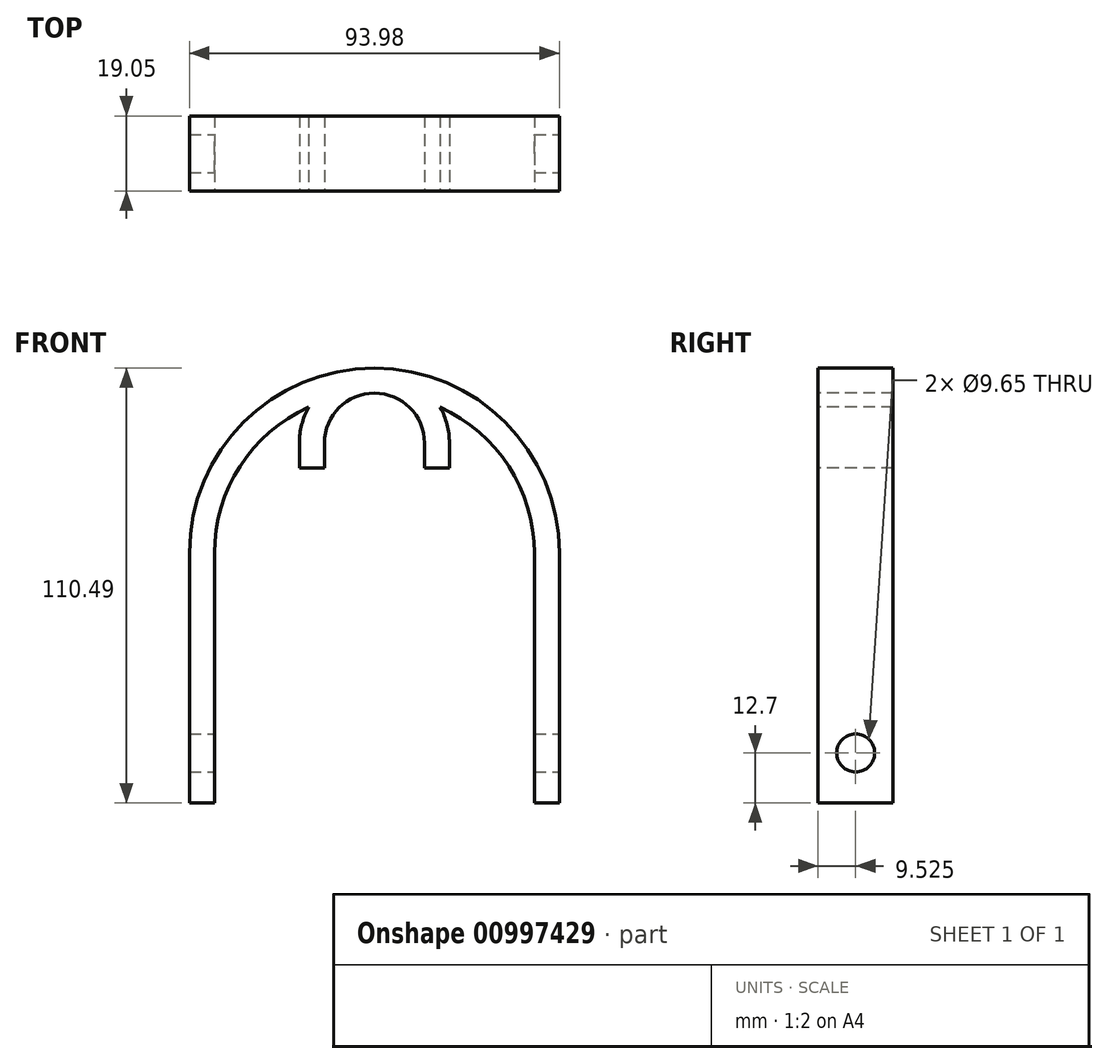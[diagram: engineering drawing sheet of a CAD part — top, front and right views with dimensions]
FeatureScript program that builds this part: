
annotation { "Feature Type Name" : "Feature", "Feature Type Description" : "" }
export const myFeature = defineFeature(function(context is Context, id is Id, definition is map)
    precondition{}
    {
        {
            var Q0;
            Q0=qCreatedBy(makeId("Front.planeOp"),FACE);
            var sketch = newSketch(context, id + "F0", { "sketchPlane" : qUnion([Q0])});
            skLineSegment(sketch, "E0", {"start": v(-40.64, 0) * mm, "end": v(40.64, 0) * mm});
            skArc(sketch, "E1", {"start": v(40.64, 0) * mm, "mid": v(0, 40.64) * mm, "end": v(-40.64, 0) * mm});
            skLineSegment(sketch, "E2.top", {"start": v(-40.64, -63.5) * mm, "end": v(40.64, -63.5) * mm});
            skLineSegment(sketch, "E2.left", {"start": v(-40.64, 0) * mm, "end": v(-40.64, -63.5) * mm});
            skLineSegment(sketch, "E2.right", {"start": v(40.64, 0) * mm, "end": v(40.64, -63.5) * mm});
            skLineSegment(sketch, "E3.0", {"start": v(47, 0) * mm, "end": v(47, -63.5) * mm});
            skArc(sketch, "E3.1", {"start": v(47, 0) * mm, "mid": v(0, 47) * mm, "end": v(-47, 0) * mm});
            skLineSegment(sketch, "E3.2", {"start": v(-47, 0) * mm, "end": v(-47, -63.5) * mm});
            skLineSegment(sketch, "E4", {"start": v(47, -63.5) * mm, "end": v(40.64, -63.5) * mm});
            skLineSegment(sketch, "E5", {"start": v(-40.64, -63.5) * mm, "end": v(-47, -63.5) * mm});
            skArc(sketch, "E6", {"start": v(12.7, 27.94) * mm, "mid": v(0, 40.64) * mm, "end": v(-12.7, 27.94) * mm});
            skArc(sketch, "E7.0", {"start": v(19.05, 27.94) * mm, "mid": v(0, 47) * mm, "end": v(-19.05, 27.94) * mm});
            skLineSegment(sketch, "E8", {"start": v(-19.05, 27.94) * mm, "end": v(-12.7, 27.94) * mm});
            skLineSegment(sketch, "E9", {"start": v(12.7, 27.94) * mm, "end": v(19.05, 27.94) * mm});
            skLineSegment(sketch, "E10.top", {"start": v(-19.05, 21.59) * mm, "end": v(-12.7, 21.59) * mm});
            skLineSegment(sketch, "E10.left", {"start": v(-19.05, 27.94) * mm, "end": v(-19.05, 21.59) * mm});
            skLineSegment(sketch, "E10.right", {"start": v(-12.7, 27.94) * mm, "end": v(-12.7, 21.59) * mm});
            skLineSegment(sketch, "E11.top", {"start": v(12.7, 21.6) * mm, "end": v(19.05, 21.6) * mm});
            skLineSegment(sketch, "E11.left", {"start": v(12.7, 27.94) * mm, "end": v(12.7, 21.6) * mm});
            skLineSegment(sketch, "E11.right", {"start": v(19.05, 27.94) * mm, "end": v(19.05, 21.6) * mm});
            skSolve(sketch);
        }
        {
            var Q0;
            {var subQ4=sQuery(id+"F0.wireOp",EDGE,"E2.left");Q0=makeQuery(id+"F0.imprint","IMPRINT",FACE,{"disambiguationData":[TD([[makeQuery(id+"F0.imprint","IMPRINT",EDGE,{"derivedFrom":subQ4}),-1.0]])]});}
            var Q1;
            {var subQ0=sQuery(id+"F0.wireOp",EDGE,"E7.0");var subQ1=sQuery(id+"F0.wireOp",EDGE,"E1");var subQ2=makeQuery(id+"F0.imprint","INTERSECT",VERTEX,{"disambiguationData":[OD(0.0)],"derivedFrom":[subQ1,subQ0]});Q1=makeQuery(id+"F0.imprint","IMPRINT",FACE,{"disambiguationData":[TD([[makeQuery(id+"F0.imprint","IMPRINT",EDGE,{"disambiguationData":[TD([[subQ2,-1.0]])],"derivedFrom":subQ1}),-1.0]])]});}
            var Q2;
            {var subQ4=sQuery(id+"F0.wireOp",EDGE,"E2.right");Q2=makeQuery(id+"F0.imprint","IMPRINT",FACE,{"disambiguationData":[TD([[makeQuery(id+"F0.imprint","IMPRINT",EDGE,{"derivedFrom":subQ4}),1.0]])]});}
            var Q3;
            {var subQ5=sQuery(id+"F0.wireOp",EDGE,"E9");Q3=makeQuery(id+"F0.imprint","IMPRINT",FACE,{"disambiguationData":[TD([[makeQuery(id+"F0.imprint","IMPRINT",EDGE,{"derivedFrom":subQ5}),1.0]])]});}
            var Q4;
            {var subQ5=sQuery(id+"F0.wireOp",EDGE,"E8");Q4=makeQuery(id+"F0.imprint","IMPRINT",FACE,{"disambiguationData":[TD([[makeQuery(id+"F0.imprint","IMPRINT",EDGE,{"derivedFrom":subQ5}),1.0]])]});}
            var Q5;
            {var subQ5=sQuery(id+"F0.wireOp",EDGE,"E8");Q5=makeQuery(id+"F0.imprint","IMPRINT",FACE,{"disambiguationData":[TD([[makeQuery(id+"F0.imprint","IMPRINT",EDGE,{"derivedFrom":subQ5}),1.0]])]});}
            var Q6;
            {var subQ5=sQuery(id+"F0.wireOp",EDGE,"E9");Q6=makeQuery(id+"F0.imprint","IMPRINT",FACE,{"disambiguationData":[TD([[makeQuery(id+"F0.imprint","IMPRINT",EDGE,{"derivedFrom":subQ5}),1.0]])]});}
            var Q7;
            Q7=makeQuery(id+"F0.imprint","IMPRINT",FACE,{"disambiguationData":[TD([[makeQuery(id+"F0.imprint","IMPRINT",EDGE,{"derivedFrom":sQuery(id+"F0.wireOp",EDGE,"E9")}),-1.0]])]});
            var Q8;
            Q8=makeQuery(id+"F0.imprint","IMPRINT",FACE,{"disambiguationData":[TD([[makeQuery(id+"F0.imprint","IMPRINT",EDGE,{"derivedFrom":sQuery(id+"F0.wireOp",EDGE,"E8")}),-1.0]])]});
            extrude(context, id + "F1", {"entities" : qUnion([Q0, Q1, Q2, Q3, Q4, Q5, Q6, Q7, Q8]), "oppositeDirection" : true, "depth" : 19.05 * mm, "offsetDistance" : 25.4 * mm});
        }
        {
            var Q0;
            Q0=makeQuery(id+"F1.opExtrude","SWEPT_FACE",FACE,{"disambiguationData":[OSD([sQuery(id+"F0.wireOp",EDGE,"E3.0")])]});
            var sketch = newSketch(context, id + "F2", { "sketchPlane" : qUnion([Q0])});
            skCircle(sketch, "E12", {"center": v(9.53, -50.8) * mm, "radius": 4.83 * mm});
            skPoint(sketch, "E13", {"position": v(9.53, -63.5) * mm});
            skSolve(sketch);
        }
        {
            var Q0;
            Q0=makeQuery(id+"F2.imprint","IMPRINT",FACE,{"disambiguationData":[TD([[makeQuery(id+"F2.imprint","IMPRINT",EDGE,{"derivedFrom":sQuery(id+"F2.wireOp",EDGE,"E12")}),1.0]])]});
            var Q1;
            Q1=sQuery(id+"F2.wireOp",EDGE,"E12");
            extrude(context, id + "F3", {"entities" : qUnion([Q0]), "operationType" : NewBodyOperationType.REMOVE, "surfaceEntities" : qUnion([Q1]), "endBound" : BoundingType.THROUGH_ALL, "oppositeDirection" : true, "depth" : 25.4 * mm, "offsetDistance" : 25.4 * mm});
        }
    });
